# Revit family: Camera-Security-Panasonic-FixedDome-Outdoor-Amba-4K_Ultra_HD_Engine-Vandal_Resistant-Waterproof-Network-SFV781L2
name_source: partatom
category: Security Devices
revit_build: Autodesk Revit 2013 (Build: 20130531_2115(x64)
units: mm (PartAtom-declared; Revit-internal decimal feet)

## types (1)
- WV-SFV781L
    Alarm Input Or Output Specification = ALARM IN1 (DAY/NIGHT IN), ALARM IN2 (ALARM OUT), ALARM IN3 (AUX OUT, DAY/NIGHT OUT)
    Angle Of View = 96
    Audio In = Yes
    Audio Out = Yes
    Communication Ports = 10Base-T / 100Base-TX, RJ-45
    Date Last Modified = September, 15, 2016
    Day Or Night = Yes
    Default Elevation = 0 "
    Description = Security Camera, Dome, Vandal Resistant, Waterproof Network, 4K Ultra HD Engine
    Diameter = 8.976 "
    Equipment Abbreviation = SC
    Family Version = 1.0.0
    HFOV Max 169 = 96.00°
    HFOV Max 43 = 100.00°
    HFOV Min 169 = 17.00°
    HFOV Min 43 = 17.00°
    Has POE = Yes
    IP Or Analog = IP
    Indoor Or Outdoor = Outdoor
    Manufacturer = Panasonic
    Minimum Illumination = 0 lx
    Model = WV-SFV781L
    Model Disclaimer = Contact Panasonic for more information
    Mounting Positions = Mount Dependent or Surface Mount
    Operational Humidity = 10% to 90% (no condensation)
    Operational Temperature = -49°F - 122°F
    Pan Max = 180.00°
    Pan Min = -180.00°
    Panning Range = -180 to +180
    Part Description = Security Camera, Dome, Vandal Resistant, Waterproof Network, 4K Ultra HD Engine
    Part Number = WV-SFV781L
    Power Active = 12.6 W
    Product Documentation Link = http://ssbu-t.psn-web.net
    Product Material = Paint - Panasonic - Silver
    Product Page URL = http://security.panasonic.com
    Provide Feedback = https://www.surveymonkey.com
    Regulatory Compliance = UL 60950-1,　UL-60950-22, C-UL, CAN/CSAC22.2 No.60950-1, CE, IEC60950-1, FCC Part 15 Class A, , ICES 003 Class A, EN55023 Class B, EN55022 Class B, EN55024
    Storage Temperature = -49°F - 149°F
    Tilt Max = 85.00°
    Tilt Min = 0.00°
    Tilting Range = 0 to +85
    URL = http://security.panasonic.com
    VFOV Max 169 = 54.00°
    VFOV Max 43 = 75.00°
    VFOV Min 169 = 9.30°
    VFOV Min 43 = 13.00°
    Vandal Resistant = Yes
    Voltage DC = 12 V
    Wide Dynamic Range = Yes
    z Base Height = 1.575 "
    z Dome Radius = 3.15 "
    z Type = 1
    z VV Origin Height Offset = 4.461 "
    z VV Viewpoint Depth Max = 2.469 "
    z VV Viewpoint Depth Min = 1.783 "

## geometry (parser evidence)
native form markers: Sweep x4
no freeform markers — native parametric forms only
